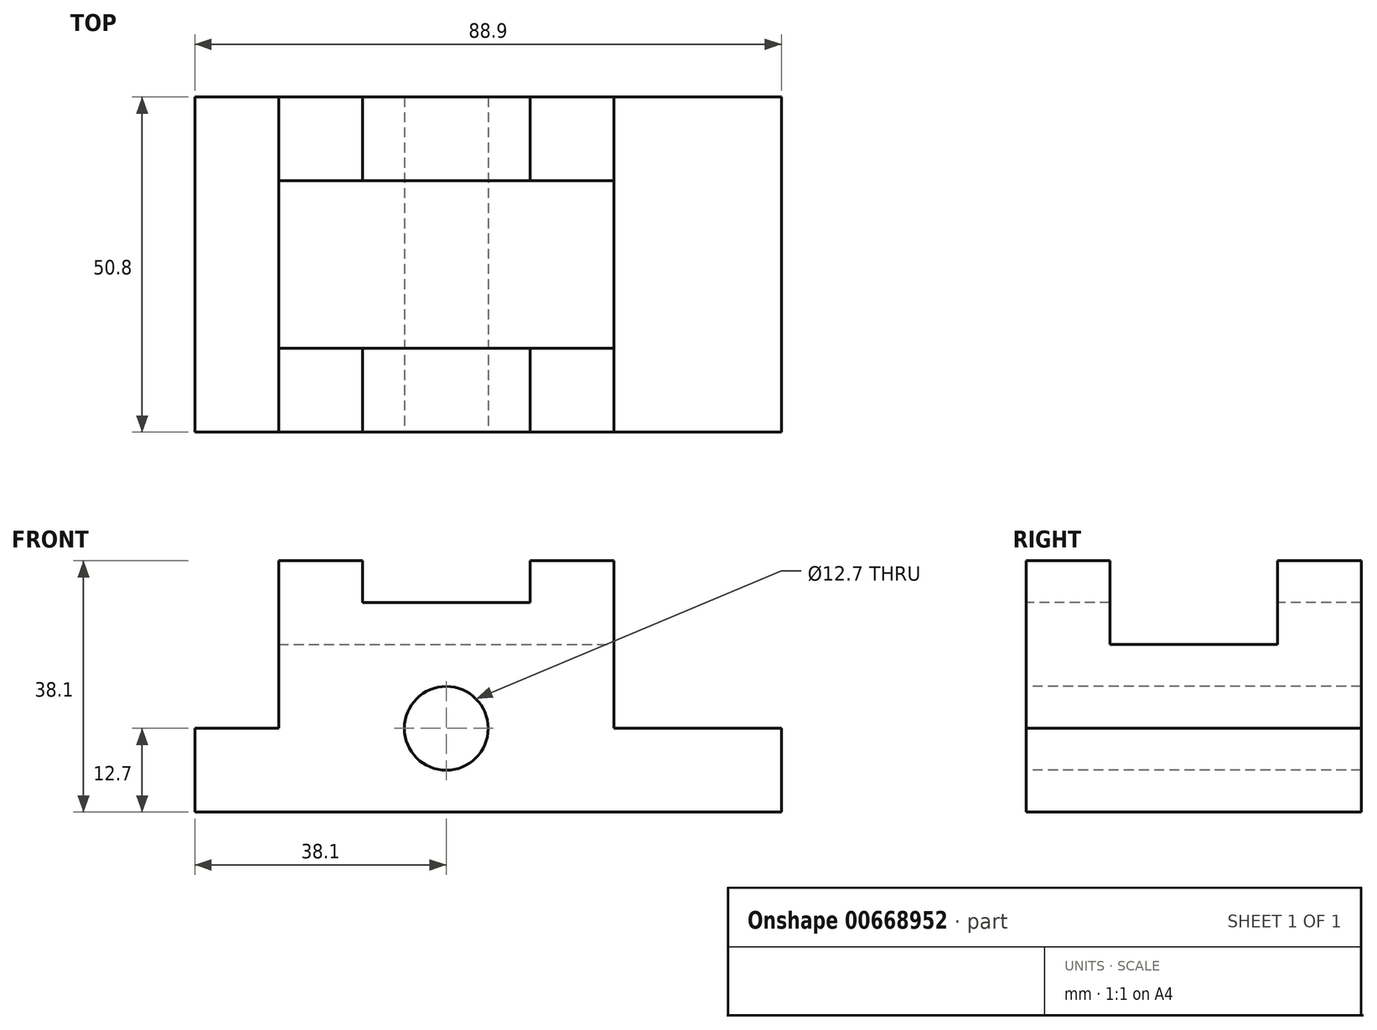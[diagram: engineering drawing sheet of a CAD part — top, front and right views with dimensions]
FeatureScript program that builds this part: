
annotation { "Feature Type Name" : "Feature", "Feature Type Description" : "" }
export const myFeature = defineFeature(function(context is Context, id is Id, definition is map)
    precondition{}
    {
        {
            var Q0;
            Q0=qCreatedBy(makeId("Front.planeOp"),FACE);
            var sketch = newSketch(context, id + "F0", { "sketchPlane" : qUnion([Q0])});
            skLineSegment(sketch, "E0.bottom", {"start": v(44.45, 19.05) * mm, "end": v(-44.45, 19.05) * mm});
            skLineSegment(sketch, "E0.top", {"start": v(44.45, -19.05) * mm, "end": v(-44.45, -19.05) * mm});
            skLineSegment(sketch, "E0.left", {"start": v(44.45, 19.05) * mm, "end": v(44.45, -19.05) * mm});
            skLineSegment(sketch, "E0.right", {"start": v(-44.45, 19.05) * mm, "end": v(-44.45, -19.05) * mm});
            skPoint(sketch, "E0.middle", {"position": v(0, 0) * mm});
            skSolve(sketch);
        }
        {
            var Q0;
            Q0 = qSketchRegion(id + "F0", true);
            extrude(context, id + "F1", {"entities" : qUnion([Q0]), "depth" : 50.8 * mm, "offsetDistance" : 25.4 * mm});
        }
        {
            var Q0;
            Q0=makeQuery(id+"F1.opExtrude","CAP_FACE",FACE,{"disambiguationData":[OSD([sQuery(id+"F0.wireOp",EDGE,"E0.bottom"),sQuery(id+"F0.wireOp",EDGE,"E0.top"),sQuery(id+"F0.wireOp",EDGE,"E0.left"),sQuery(id+"F0.wireOp",EDGE,"E0.right")])],"isStart":false});
            var sketch = newSketch(context, id + "F2", { "sketchPlane" : qUnion([Q0])});
            skLineSegment(sketch, "E1.bottom", {"start": v(-44.45, 19.05) * mm, "end": v(-31.75, 19.05) * mm});
            skLineSegment(sketch, "E1.top", {"start": v(-44.45, -6.35) * mm, "end": v(-31.75, -6.35) * mm});
            skLineSegment(sketch, "E1.left", {"start": v(-44.45, 19.05) * mm, "end": v(-44.45, -6.35) * mm});
            skLineSegment(sketch, "E1.right", {"start": v(-31.75, 19.05) * mm, "end": v(-31.75, -6.35) * mm});
            skSolve(sketch);
        }
        {
            var Q0;
            Q0 = qSketchRegion(id + "F2", true);
            extrude(context, id + "F3", {"entities" : qUnion([Q0]), "operationType" : NewBodyOperationType.REMOVE, "endBound" : BoundingType.THROUGH_ALL, "oppositeDirection" : true, "depth" : 25.4 * mm, "offsetDistance" : 25.4 * mm});
        }
        {
            var Q0;
            Q0=makeQuery(id+"F1.opExtrude","CAP_FACE",FACE,{"disambiguationData":[OSD([sQuery(id+"F0.wireOp",EDGE,"E0.bottom"),sQuery(id+"F0.wireOp",EDGE,"E0.top"),sQuery(id+"F0.wireOp",EDGE,"E0.left"),sQuery(id+"F0.wireOp",EDGE,"E0.right")])],"isStart":false});
            var sketch = newSketch(context, id + "F4", { "sketchPlane" : qUnion([Q0])});
            skLineSegment(sketch, "E2.bottom", {"start": v(44.45, 19.05) * mm, "end": v(19.05, 19.05) * mm});
            skLineSegment(sketch, "E2.top", {"start": v(44.45, -6.35) * mm, "end": v(19.05, -6.35) * mm});
            skLineSegment(sketch, "E2.left", {"start": v(44.45, 19.05) * mm, "end": v(44.45, -6.35) * mm});
            skLineSegment(sketch, "E2.right", {"start": v(19.05, 19.05) * mm, "end": v(19.05, -6.35) * mm});
            skSolve(sketch);
        }
        {
            var Q0;
            Q0 = qSketchRegion(id + "F4", true);
            extrude(context, id + "F5", {"entities" : qUnion([Q0]), "operationType" : NewBodyOperationType.REMOVE, "endBound" : BoundingType.THROUGH_ALL, "oppositeDirection" : true, "depth" : 25.4 * mm, "offsetDistance" : 25.4 * mm});
        }
        {
            var Q0;
            Q0=makeQuery(id+"F1.opExtrude","CAP_FACE",FACE,{"disambiguationData":[OSD([sQuery(id+"F0.wireOp",EDGE,"E0.bottom"),sQuery(id+"F0.wireOp",EDGE,"E0.top"),sQuery(id+"F0.wireOp",EDGE,"E0.left"),sQuery(id+"F0.wireOp",EDGE,"E0.right")])],"isStart":false});
            var sketch = newSketch(context, id + "F6", { "sketchPlane" : qUnion([Q0])});
            skLineSegment(sketch, "E3.bottom", {"start": v(-19.05, 19.05) * mm, "end": v(6.35, 19.05) * mm});
            skLineSegment(sketch, "E3.top", {"start": v(-19.05, 12.7) * mm, "end": v(6.35, 12.7) * mm});
            skLineSegment(sketch, "E3.left", {"start": v(-19.05, 19.05) * mm, "end": v(-19.05, 12.7) * mm});
            skLineSegment(sketch, "E3.right", {"start": v(6.35, 19.05) * mm, "end": v(6.35, 12.7) * mm});
            skSolve(sketch);
        }
        {
            var Q0;
            Q0 = qSketchRegion(id + "F6", true);
            extrude(context, id + "F7", {"entities" : qUnion([Q0]), "operationType" : NewBodyOperationType.REMOVE, "endBound" : BoundingType.THROUGH_ALL, "oppositeDirection" : true, "depth" : 25.4 * mm, "offsetDistance" : 25.4 * mm});
        }
        {
            var Q0;
            Q0=makeQuery(id+"F1.opExtrude","CAP_FACE",FACE,{"disambiguationData":[OSD([sQuery(id+"F0.wireOp",EDGE,"E0.bottom"),sQuery(id+"F0.wireOp",EDGE,"E0.top"),sQuery(id+"F0.wireOp",EDGE,"E0.left"),sQuery(id+"F0.wireOp",EDGE,"E0.right")])],"isStart":false});
            var sketch = newSketch(context, id + "F8", { "sketchPlane" : qUnion([Q0])});
            skCircle(sketch, "E4", {"center": v(-6.35, -6.35) * mm, "radius": 6.35 * mm});
            skSolve(sketch);
        }
        {
            var Q0;
            Q0 = qSketchRegion(id + "F8", true);
            extrude(context, id + "F9", {"entities" : qUnion([Q0]), "operationType" : NewBodyOperationType.REMOVE, "endBound" : BoundingType.THROUGH_ALL, "oppositeDirection" : true, "depth" : 25.4 * mm, "offsetDistance" : 25.4 * mm});
        }
        {
            var Q0;
            Q0=makeQuery(id+"F5.boolean.opBoolean","COPY",FACE,{"derivedFrom":makeQuery(id+"F5.opExtrude","SWEPT_FACE",FACE,{"disambiguationData":[OSD([sQuery(id+"F4.wireOp",EDGE,"E2.right")])]})});
            var sketch = newSketch(context, id + "F10", { "sketchPlane" : qUnion([Q0])});
            skLineSegment(sketch, "E5.bottom", {"start": v(-38.1, 19.05) * mm, "end": v(-12.7, 19.05) * mm});
            skLineSegment(sketch, "E5.top", {"start": v(-38.1, 6.35) * mm, "end": v(-12.7, 6.35) * mm});
            skLineSegment(sketch, "E5.left", {"start": v(-38.1, 19.05) * mm, "end": v(-38.1, 6.35) * mm});
            skLineSegment(sketch, "E5.right", {"start": v(-12.7, 19.05) * mm, "end": v(-12.7, 6.35) * mm});
            skSolve(sketch);
        }
        {
            var Q0;
            Q0 = qSketchRegion(id + "F10", true);
            extrude(context, id + "F11", {"entities" : qUnion([Q0]), "operationType" : NewBodyOperationType.REMOVE, "endBound" : BoundingType.THROUGH_ALL, "oppositeDirection" : true, "depth" : 25.4 * mm, "offsetDistance" : 25.4 * mm});
        }
    });
